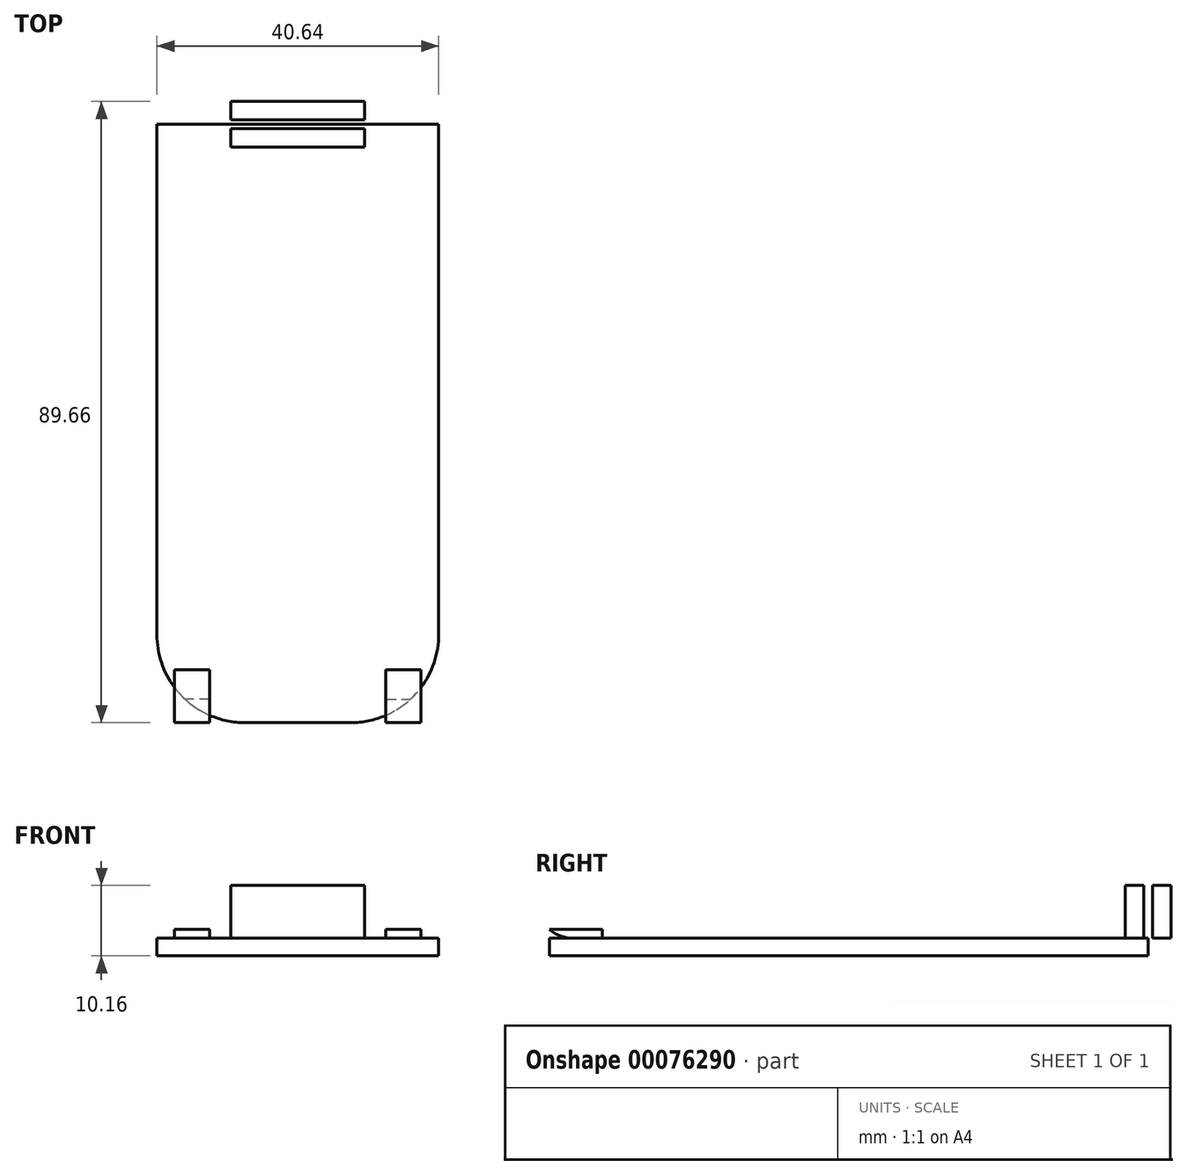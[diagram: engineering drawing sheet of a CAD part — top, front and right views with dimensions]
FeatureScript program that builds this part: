
annotation { "Feature Type Name" : "Feature", "Feature Type Description" : "" }
export const myFeature = defineFeature(function(context is Context, id is Id, definition is map)
    precondition{}
    {
        {
            var Q0;
            Q0=qCreatedBy(makeId("Top.planeOp"),FACE);
            var sketch = newSketch(context, id + "F0", { "sketchPlane" : qUnion([Q0])});
            skLineSegment(sketch, "E0.bottom", {"start": v(20.32, 43.18) * mm, "end": v(-20.32, 43.18) * mm});
            skLineSegment(sketch, "E0.top", {"start": v(7.62, -43.18) * mm, "end": v(-7.62, -43.18) * mm});
            skLineSegment(sketch, "E0.left", {"start": v(20.32, 43.18) * mm, "end": v(20.32, -30.48) * mm});
            skLineSegment(sketch, "E0.right", {"start": v(-20.32, 43.18) * mm, "end": v(-20.32, -30.48) * mm});
            skPoint(sketch, "E0.middle", {"position": v(0, 0) * mm});
            skPoint(sketch, "E1.visualSharp", {"position": v(-20.32, -43.18) * mm});
            skArc(sketch, "E1.filletArc", {"start": v(-20.32, -30.48) * mm, "mid": v(-16.6, -39.46) * mm, "end": v(-7.62, -43.18) * mm});
            skPoint(sketch, "E2.visualSharp", {"position": v(20.32, -43.18) * mm});
            skArc(sketch, "E2.filletArc", {"start": v(7.62, -43.18) * mm, "mid": v(16.6, -39.46) * mm, "end": v(20.32, -30.48) * mm});
            skSolve(sketch);
        }
        {
            var Q0;
            Q0=makeQuery(id+"F0.imprint","IMPRINT",FACE,{"disambiguationData":[TD([[makeQuery(id+"F0.imprint","IMPRINT",EDGE,{"derivedFrom":sQuery(id+"F0.wireOp",EDGE,"E0.bottom")}),1.0]])]});
            extrude(context, id + "F1", {"entities" : qUnion([Q0]), "depth" : 2.54 * mm});
        }
        {
            var Q0;
            Q0=makeQuery(id+"F1.opExtrude","CAP_FACE",FACE,{"disambiguationData":[OSD([sQuery(id+"F0.wireOp",EDGE,"E0.bottom"),sQuery(id+"F0.wireOp",EDGE,"E0.top"),sQuery(id+"F0.wireOp",EDGE,"E0.left"),sQuery(id+"F0.wireOp",EDGE,"E0.right"),sQuery(id+"F0.wireOp",EDGE,"E1.filletArc"),sQuery(id+"F0.wireOp",EDGE,"E2.filletArc")])],"isStart":false});
            var sketch = newSketch(context, id + "F2", { "sketchPlane" : qUnion([Q0])});
            skPoint(sketch, "E3.middle", {"position": v(0, -43.18) * mm});
            skLineSegment(sketch, "E4", {"start": v(0, -43.18) * mm, "end": v(-12.7, -43.18) * mm, "construction": true});
            skLineSegment(sketch, "E5", {"start": v(0, -43.18) * mm, "end": v(12.7, -43.18) * mm, "construction": true});
            skLineSegment(sketch, "E6.bottom", {"start": v(-12.7, -43.18) * mm, "end": v(-17.78, -43.18) * mm});
            skLineSegment(sketch, "E6.top", {"start": v(-12.7, -35.56) * mm, "end": v(-17.78, -35.56) * mm});
            skLineSegment(sketch, "E6.left", {"start": v(-12.7, -43.18) * mm, "end": v(-12.7, -35.56) * mm});
            skLineSegment(sketch, "E6.right", {"start": v(-17.78, -43.18) * mm, "end": v(-17.78, -35.56) * mm});
            skLineSegment(sketch, "E7", {"start": v(0, -19.56) * mm, "end": v(0, -60.39) * mm});
            skLineSegment(sketch, "E8.MirrorCS", {"start": v(12.7, -43.18) * mm, "end": v(12.7, -35.56) * mm});
            skLineSegment(sketch, "E9.MirrorCS", {"start": v(12.7, -35.56) * mm, "end": v(17.78, -35.56) * mm});
            skLineSegment(sketch, "E10.MirrorCS", {"start": v(17.78, -43.18) * mm, "end": v(17.78, -35.56) * mm});
            skLineSegment(sketch, "E11.MirrorCS", {"start": v(12.7, -43.18) * mm, "end": v(17.78, -43.18) * mm});
            skLineSegment(sketch, "E12.bottom", {"start": v(9.65, 39.88) * mm, "end": v(-9.65, 39.88) * mm});
            skLineSegment(sketch, "E12.top", {"start": v(9.65, 46.48) * mm, "end": v(-9.65, 46.48) * mm});
            skLineSegment(sketch, "E12.left", {"start": v(9.65, 39.88) * mm, "end": v(9.65, 46.48) * mm});
            skLineSegment(sketch, "E12.right", {"start": v(-9.65, 39.88) * mm, "end": v(-9.65, 46.48) * mm});
            skPoint(sketch, "E12.middle", {"position": v(0, 43.18) * mm});
            skLineSegment(sketch, "E13.bottom", {"start": v(9.65, 43.81) * mm, "end": v(-9.65, 43.81) * mm});
            skLineSegment(sketch, "E13.top", {"start": v(9.65, 42.54) * mm, "end": v(-9.65, 42.54) * mm});
            skLineSegment(sketch, "E13.left", {"start": v(9.65, 43.81) * mm, "end": v(9.65, 42.54) * mm});
            skLineSegment(sketch, "E13.right", {"start": v(-9.65, 43.81) * mm, "end": v(-9.65, 42.54) * mm});
            skSolve(sketch);
        }
        {
            var Q0;
            {var subQ0=sQuery(id+"F2.wireOp",EDGE,"E6.bottom");Q0=makeQuery(id+"F2.imprint","IMPRINT",FACE,{"disambiguationData":[TD([[makeQuery(id+"F2.imprint","IMPRINT",EDGE,{"derivedFrom":subQ0}),-1.0]])]});}
            var Q1;
            {var subQ0=sQuery(id+"F2.wireOp",EDGE,"E6.top");Q1=makeQuery(id+"F2.imprint","IMPRINT",FACE,{"disambiguationData":[TD([[makeQuery(id+"F2.imprint","IMPRINT",EDGE,{"derivedFrom":subQ0}),1.0]])]});}
            var Q2;
            {var subQ0=sQuery(id+"F2.wireOp",EDGE,"E11.MirrorCS");Q2=makeQuery(id+"F2.imprint","IMPRINT",FACE,{"disambiguationData":[TD([[makeQuery(id+"F2.imprint","IMPRINT",EDGE,{"derivedFrom":subQ0}),1.0]])]});}
            var Q3;
            {var subQ0=sQuery(id+"F2.wireOp",EDGE,"E9.MirrorCS");Q3=makeQuery(id+"F2.imprint","IMPRINT",FACE,{"disambiguationData":[TD([[makeQuery(id+"F2.imprint","IMPRINT",EDGE,{"derivedFrom":subQ0}),-1.0]])]});}
            extrude(context, id + "F3", {"entities" : qUnion([Q0, Q1, Q2, Q3]), "operationType" : NewBodyOperationType.ADD, "depth" : 1.27 * mm});
        }
        {
            var Q0;
            Q0=makeQuery(id+"F3.opExtrude","CAP_EDGE",EDGE,{"disambiguationData":[OSD([sQuery(id+"F2.wireOp",EDGE,"E9.MirrorCS")])],"isStart":true});
            var Q1;
            Q1=makeQuery(id+"F3.opExtrude","CAP_EDGE",EDGE,{"disambiguationData":[OSD([sQuery(id+"F2.wireOp",EDGE,"E6.top")])],"isStart":true});
            var Q2;
            Q2=makeQuery(id+"F3.opExtrude","CAP_EDGE",EDGE,{"disambiguationData":[OSD([sQuery(id+"F2.wireOp",EDGE,"E11.MirrorCS")])],"isStart":true});
            var Q3;
            Q3=makeQuery(id+"F3.opExtrude","CAP_EDGE",EDGE,{"disambiguationData":[OSD([sQuery(id+"F2.wireOp",EDGE,"E6.bottom")])],"isStart":true});
            fillet(context, id + "F4", {"entities" : qUnion([Q0, Q1, Q2, Q3]), "radius" : 5.08 * mm, "tangentPropagation" : true, "allowEdgeOverflow" : false});
        }
        {
            var Q0;
            {var subQ0=sQuery(id+"F2.wireOp",EDGE,"E12.bottom");Q0=makeQuery(id+"F2.imprint","IMPRINT",FACE,{"disambiguationData":[TD([[makeQuery(id+"F2.imprint","IMPRINT",EDGE,{"derivedFrom":subQ0}),-1.0]])]});}
            var Q1;
            {var subQ0=sQuery(id+"F2.wireOp",EDGE,"E12.top");Q1=makeQuery(id+"F2.imprint","IMPRINT",FACE,{"disambiguationData":[TD([[makeQuery(id+"F2.imprint","IMPRINT",EDGE,{"derivedFrom":subQ0}),1.0]])]});}
            extrude(context, id + "F5", {"entities" : qUnion([Q0, Q1]), "operationType" : NewBodyOperationType.ADD, "depth" : 7.62 * mm});
        }
    });
